# Revit family: Door_Access_Duct_Acudor_HD-5070
name_source: partatom
category: Duct Accessories
units: mm (PartAtom-declared; Revit-internal decimal feet)

## family parameters
Always vertical = No
Cut with Voids When Loaded = No
Part Type = Attaches To
Round Connector Dimension = Use Diameter
Shared = No
Work Plane-Based = Yes

## types (9) — shared parameters
Default Elevation = 0' - 0"
Description = Acudor Duct Access Door - HD-5070 as Specified
Model = HD-5070
Revision = R1_01-2014
Unit Depth = 0' - 1"
zero-valued in all types: Expected Lifespan (Years), Maintenance Schedule (Months), Warranty Duration (Years)

## per-type parameters (varying)
| type | Door Height | Door Width | Opening Height | Opening Width | Unit Height | Unit Weight | Unit Width |
| 24 x 24 Nom | 1' - 11 1/2" | 1' - 11 1/2" | 1' - 10 3/4" | 1' - 10 3/4" | 2' - 0" | 12 | 2' - 0" |
| 20 x 20 Nom | 1' - 7 1/2" | 1' - 7 1/2" | 1' - 6 3/4" | 1' - 6 3/4" | 1' - 8" | 9 | 1' - 8" |
| 18 x 18 Nom | 1' - 5 1/2" | 1' - 5 1/2" | 1' - 4 3/4" | 1' - 4 3/4" | 1' - 6" | 6.75 | 1' - 6" |
| 16 x 16 Nom | 1' - 3 1/2" | 1' - 3 1/2" | 1' - 2 3/4" | 1' - 2 3/4" | 1' - 4" | 5.25 | 1' - 4" |
| 14 x 14 Nom | 1' - 1 1/2" | 1' - 1 1/2" | 1' - 0 3/4" | 1' - 0 3/4" | 1' - 2" | 4.75 | 1' - 2" |
| 12 x 12 Nom | 0' - 11 1/2" | 0' - 11 1/2" | 0' - 10 3/4" | 0' - 10 3/4" | 1' - 0" | 3.75 | 1' - 0" |
| 10 x 10 Nom | 0' - 9 1/2" | 0' - 9 1/2" | 0' - 8 3/4" | 0' - 8 3/4" | 0' - 10" | 2.75 | 0' - 10" |
| 8 x 8 Nom | 0' - 7 1/2" | 0' - 7 1/2" | 0' - 6 3/4" | 0' - 6 3/4" | 0' - 8" | 1.75 | 0' - 8" |
| 6 x 6 Nom | 0' - 5 1/2" | 0' - 5 1/2" | 0' - 4 3/4" | 0' - 4 3/4" | 0' - 6" | 1.25 | 0' - 6" |

## geometry (parser evidence)
native form markers: Sweep x2
no freeform markers — native parametric forms only
